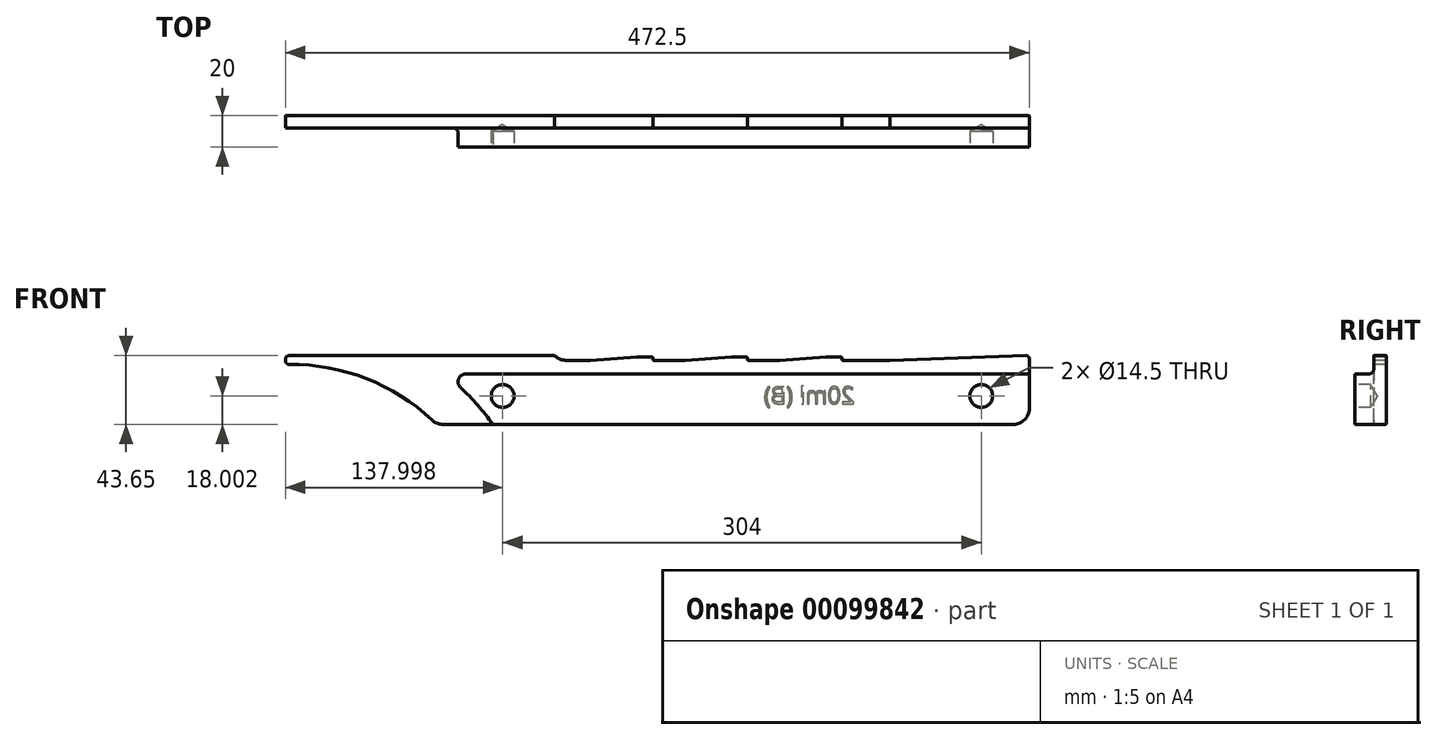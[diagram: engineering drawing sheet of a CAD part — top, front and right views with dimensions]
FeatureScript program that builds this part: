
annotation { "Feature Type Name" : "Feature", "Feature Type Description" : "" }
export const myFeature = defineFeature(function(context is Context, id is Id, definition is map)
    precondition{}
    {
        {
            var Q0;
            Q0=qCreatedBy(makeId("Front.planeOp"),FACE);
            var sketch = newSketch(context, id + "F0", { "sketchPlane" : qUnion([Q0])});
            skFitSpline(sketch, "E0", {"points": [v(183.92, 49.12) * mm, v(184, 49.11) * mm, v(184.18, 49.07) * mm, v(184.37, 48.88) * mm, v(184.42, 48.7) * mm, v(184.42, 48.62) * mm]});
            skLineSegment(sketch, "E1", {"start": v(184.42, 48.62) * mm, "end": v(184.42, 29.12) * mm});
            skLineSegment(sketch, "E2", {"start": v(184.42, 29.12) * mm, "end": v(161.17, 29.12) * mm});
            skLineSegment(sketch, "E3", {"start": v(161.17, 29.12) * mm, "end": v(161.17, 43.12) * mm});
            skLineSegment(sketch, "E4", {"start": v(161.17, 43.12) * mm, "end": v(146.67, 43.12) * mm});
            skLineSegment(sketch, "E5", {"start": v(146.67, 43.12) * mm, "end": v(146.67, 29.12) * mm});
            skLineSegment(sketch, "E6", {"start": v(146.67, 29.12) * mm, "end": v(129.51, 29.12) * mm});
            skFitSpline(sketch, "E7", {"points": [v(129.51, 29.12) * mm, v(128.82, 30.1) * mm, v(127.65, 32.27) * mm, v(126.67, 36.03) * mm, v(126.5, 40.27) * mm, v(127.13, 44.76) * mm, v(128.15, 47.72) * mm, v(128.8, 49.12) * mm]});
            skLineSegment(sketch, "E8", {"start": v(128.8, 49.12) * mm, "end": v(183.92, 49.12) * mm});
            skLineSegment(sketch, "E9", {"start": v(-288.08, -225.1) * mm, "end": v(-288.08, -225.75) * mm});
            skLineSegment(sketch, "E10", {"start": v(-287.58, -225.1) * mm, "end": v(-287.58, -225.75) * mm});
            skLineSegment(sketch, "E11", {"start": v(-285.58, -227.75) * mm, "end": v(-285.58, -228.25) * mm});
            skLineSegment(sketch, "E12", {"start": v(-285.58, -223.1) * mm, "end": v(-285.58, -222.6) * mm});
            skLineSegment(sketch, "E13", {"start": v(-284.08, -223.1) * mm, "end": v(-284.08, -222.6) * mm});
            skLineSegment(sketch, "E14", {"start": v(81.08, -203.54) * mm, "end": v(82.13, -203.33) * mm});
            skLineSegment(sketch, "E15", {"start": v(71.5, -203.54) * mm, "end": v(72.54, -203.33) * mm});
            skLineSegment(sketch, "E16", {"start": v(71.5, -195.67) * mm, "end": v(70.46, -195.88) * mm});
            skLineSegment(sketch, "E17", {"start": v(71.5, -204.6) * mm, "end": v(72.75, -204.39) * mm});
            skLineSegment(sketch, "E18", {"start": v(82.33, -204.39) * mm, "end": v(80.88, -204.6) * mm});
            skLineSegment(sketch, "E19", {"start": v(-285.58, -228.25) * mm, "end": v(-117.08, -228.25) * mm});
            skLineSegment(sketch, "E20", {"start": v(24.42, -194.81) * mm, "end": v(25.46, -194.6) * mm});
            skLineSegment(sketch, "E21", {"start": v(71.5, -194.6) * mm, "end": v(70.25, -194.81) * mm});
            skLineSegment(sketch, "E22", {"start": v(-285.58, -227.75) * mm, "end": v(-117.29, -227.75) * mm});
            skLineSegment(sketch, "E23", {"start": v(-64.42, -227.25) * mm, "end": v(-55.08, -227.25) * mm});
            skLineSegment(sketch, "E24", {"start": v(-4.42, -227.25) * mm, "end": v(4.92, -227.25) * mm});
            skLineSegment(sketch, "E25", {"start": v(55.58, -227.25) * mm, "end": v(64.92, -227.25) * mm});
            skLineSegment(sketch, "E26", {"start": v(-64.42, -226.75) * mm, "end": v(-54.58, -226.75) * mm});
            skLineSegment(sketch, "E27", {"start": v(-4.42, -226.75) * mm, "end": v(5.42, -226.75) * mm});
            skLineSegment(sketch, "E28", {"start": v(55.58, -226.75) * mm, "end": v(65.42, -226.75) * mm});
            skLineSegment(sketch, "E29", {"start": v(183.92, -226.25) * mm, "end": v(184.42, -226.25) * mm});
            skLineSegment(sketch, "E30", {"start": v(-55.08, -225.75) * mm, "end": v(-54.58, -225.75) * mm});
            skLineSegment(sketch, "E31", {"start": v(4.92, -225.75) * mm, "end": v(5.42, -225.75) * mm});
            skLineSegment(sketch, "E32", {"start": v(64.92, -225.75) * mm, "end": v(65.42, -225.75) * mm});
            skLineSegment(sketch, "E33", {"start": v(-287.58, -225.75) * mm, "end": v(-288.08, -225.75) * mm});
            skLineSegment(sketch, "E34", {"start": v(-109.94, -225.25) * mm, "end": v(-94.75, -225.25) * mm});
            skLineSegment(sketch, "E35", {"start": v(-54.08, -225.25) * mm, "end": v(-34.75, -225.25) * mm});
            skLineSegment(sketch, "E36", {"start": v(5.92, -225.25) * mm, "end": v(25.25, -225.25) * mm});
            skLineSegment(sketch, "E37", {"start": v(65.92, -225.25) * mm, "end": v(95.92, -225.25) * mm});
            skLineSegment(sketch, "E38", {"start": v(-287.58, -225.1) * mm, "end": v(-288.08, -225.1) * mm});
            skLineSegment(sketch, "E39", {"start": v(-109.94, -224.75) * mm, "end": v(-94.75, -224.75) * mm});
            skLineSegment(sketch, "E40", {"start": v(-54.08, -224.75) * mm, "end": v(-34.75, -224.75) * mm});
            skLineSegment(sketch, "E41", {"start": v(5.92, -224.75) * mm, "end": v(25.25, -224.75) * mm});
            skLineSegment(sketch, "E42", {"start": v(65.92, -224.75) * mm, "end": v(95.93, -224.75) * mm});
            skLineSegment(sketch, "E43", {"start": v(-284.08, -223.1) * mm, "end": v(-285.58, -223.1) * mm});
            skLineSegment(sketch, "E44", {"start": v(-284.08, -222.6) * mm, "end": v(-285.58, -222.6) * mm});
            skLineSegment(sketch, "E45", {"start": v(-94.75, -225.25) * mm, "end": v(-94.42, -225.26) * mm});
            skLineSegment(sketch, "E46", {"start": v(-34.75, -225.25) * mm, "end": v(-34.42, -225.26) * mm});
            skLineSegment(sketch, "E47", {"start": v(25.25, -225.25) * mm, "end": v(25.58, -225.26) * mm});
            skLineSegment(sketch, "E48", {"start": v(95.92, -225.25) * mm, "end": v(182.87, -228.2) * mm});
            skLineSegment(sketch, "E49", {"start": v(95.93, -224.75) * mm, "end": v(182.82, -227.7) * mm});
            skLineSegment(sketch, "E50", {"start": v(-94.42, -225.26) * mm, "end": v(-64.75, -227.24) * mm});
            skLineSegment(sketch, "E51", {"start": v(-94.38, -224.76) * mm, "end": v(-64.71, -226.74) * mm});
            skLineSegment(sketch, "E52", {"start": v(-34.42, -225.26) * mm, "end": v(-4.75, -227.24) * mm});
            skLineSegment(sketch, "E53", {"start": v(-34.38, -224.76) * mm, "end": v(-4.71, -226.74) * mm});
            skLineSegment(sketch, "E54", {"start": v(25.58, -225.26) * mm, "end": v(55.25, -227.24) * mm});
            skLineSegment(sketch, "E55", {"start": v(25.62, -224.76) * mm, "end": v(55.29, -226.74) * mm});
            skLineSegment(sketch, "E56", {"start": v(-194.7, -187.68) * mm, "end": v(-195.04, -187.32) * mm});
            skLineSegment(sketch, "E57", {"start": v(80.88, -204.6) * mm, "end": v(80.04, -204.6) * mm});
            skLineSegment(sketch, "E58", {"start": v(46.7, -204.6) * mm, "end": v(45.67, -204.6) * mm});
            skLineSegment(sketch, "E59", {"start": v(30.46, -204.6) * mm, "end": v(25.46, -204.6) * mm});
            skLineSegment(sketch, "E60", {"start": v(21.08, -204.6) * mm, "end": v(20.25, -204.6) * mm});
            skLineSegment(sketch, "E61", {"start": v(32.13, -204.6) * mm, "end": v(32.96, -204.6) * mm});
            skLineSegment(sketch, "E62", {"start": v(80.25, -203.54) * mm, "end": v(81.08, -203.54) * mm});
            skLineSegment(sketch, "E63", {"start": v(25.25, -203.33) * mm, "end": v(29.2, -203.33) * mm});
            skLineSegment(sketch, "E64", {"start": v(83.17, -202.26) * mm, "end": v(84.2, -202.26) * mm});
            skLineSegment(sketch, "E65", {"start": v(56.08, -201.41) * mm, "end": v(55.04, -201.41) * mm});
            skLineSegment(sketch, "E66", {"start": v(54, -201.41) * mm, "end": v(53.17, -201.41) * mm});
            skLineSegment(sketch, "E67", {"start": v(50.67, -201.41) * mm, "end": v(49.83, -201.41) * mm});
            skLineSegment(sketch, "E68", {"start": v(50.25, -200.56) * mm, "end": v(50.88, -200.56) * mm});
            skLineSegment(sketch, "E69", {"start": v(53.58, -200.56) * mm, "end": v(54, -200.56) * mm});
            skLineSegment(sketch, "E70", {"start": v(29.2, -200.35) * mm, "end": v(25.25, -200.35) * mm});
            skLineSegment(sketch, "E71", {"start": v(29.2, -199.07) * mm, "end": v(25.25, -199.07) * mm});
            skLineSegment(sketch, "E72", {"start": v(25.25, -195.88) * mm, "end": v(29.2, -195.88) * mm});
            skLineSegment(sketch, "E73", {"start": v(82.75, -195.67) * mm, "end": v(76.92, -195.67) * mm});
            skLineSegment(sketch, "E74", {"start": v(25.46, -194.6) * mm, "end": v(30.46, -194.6) * mm});
            skLineSegment(sketch, "E75", {"start": v(45.67, -194.6) * mm, "end": v(46.7, -194.6) * mm});
            skLineSegment(sketch, "E76", {"start": v(48.38, -194.6) * mm, "end": v(49.42, -194.6) * mm});
            skLineSegment(sketch, "E77", {"start": v(51.7, -194.6) * mm, "end": v(52.75, -194.6) * mm});
            skLineSegment(sketch, "E78", {"start": v(55.04, -194.6) * mm, "end": v(56.08, -194.6) * mm});
            skLineSegment(sketch, "E79", {"start": v(76.92, -194.6) * mm, "end": v(84.42, -194.6) * mm});
            skLineSegment(sketch, "E80", {"start": v(183.92, -194.6) * mm, "end": v(184.42, -194.6) * mm});
            skLineSegment(sketch, "E81", {"start": v(32.96, -193.33) * mm, "end": v(32.13, -193.33) * mm});
            skLineSegment(sketch, "E82", {"start": v(20.25, -193.33) * mm, "end": v(21.08, -193.33) * mm});
            skLineSegment(sketch, "E83", {"start": v(174.42, -185.1) * mm, "end": v(-188.19, -185.1) * mm});
            skLineSegment(sketch, "E84", {"start": v(174.42, -184.6) * mm, "end": v(-188.19, -184.6) * mm});
            skLineSegment(sketch, "E85", {"start": v(-117.18, -228) * mm, "end": v(-117.01, -228.18) * mm});
            skLineSegment(sketch, "E86", {"start": v(70.25, -204.39) * mm, "end": v(71.5, -204.6) * mm});
            skLineSegment(sketch, "E87", {"start": v(80.04, -204.6) * mm, "end": v(78.8, -204.39) * mm});
            skLineSegment(sketch, "E88", {"start": v(72.75, -194.81) * mm, "end": v(71.5, -194.6) * mm});
            skLineSegment(sketch, "E89", {"start": v(25.46, -204.6) * mm, "end": v(24.42, -204.39) * mm});
            skLineSegment(sketch, "E90", {"start": v(70.46, -203.33) * mm, "end": v(71.5, -203.54) * mm});
            skLineSegment(sketch, "E91", {"start": v(79.2, -203.33) * mm, "end": v(80.25, -203.54) * mm});
            skLineSegment(sketch, "E92", {"start": v(-188.19, -185.1) * mm, "end": v(-188.19, -184.6) * mm});
            skLineSegment(sketch, "E93", {"start": v(72.54, -195.88) * mm, "end": v(71.5, -195.67) * mm});
            skLineSegment(sketch, "E94", {"start": v(24.63, -203.11) * mm, "end": v(25.25, -203.33) * mm});
            skLineSegment(sketch, "E95", {"start": v(25.25, -199.07) * mm, "end": v(24.63, -198.86) * mm});
            skLineSegment(sketch, "E96", {"start": v(49.83, -201.41) * mm, "end": v(49.2, -201.2) * mm});
            skLineSegment(sketch, "E97", {"start": v(53.17, -201.41) * mm, "end": v(52.54, -201.2) * mm});
            skLineSegment(sketch, "E98", {"start": v(24, -199.7) * mm, "end": v(23.58, -199.5) * mm});
            skLineSegment(sketch, "E99", {"start": v(49.83, -200.35) * mm, "end": v(50.25, -200.56) * mm});
            skLineSegment(sketch, "E100", {"start": v(53.17, -200.35) * mm, "end": v(53.58, -200.56) * mm});
            skLineSegment(sketch, "E101", {"start": v(78.8, -204.39) * mm, "end": v(77.96, -203.96) * mm});
            skLineSegment(sketch, "E102", {"start": v(24.42, -204.39) * mm, "end": v(23.58, -203.75) * mm});
            skLineSegment(sketch, "E103", {"start": v(-109.94, -224.75) * mm, "end": v(-109.94, -225.25) * mm});
            skLineSegment(sketch, "E104", {"start": v(69.2, -203.75) * mm, "end": v(70.25, -204.39) * mm});
            skLineSegment(sketch, "E105", {"start": v(73.8, -195.45) * mm, "end": v(72.75, -194.81) * mm});
            skLineSegment(sketch, "E106", {"start": v(69.83, -202.9) * mm, "end": v(70.46, -203.33) * mm});
            skLineSegment(sketch, "E107", {"start": v(78.58, -202.9) * mm, "end": v(79.2, -203.33) * mm});
            skLineSegment(sketch, "E108", {"start": v(-94.75, -224.75) * mm, "end": v(-94.75, -225.25) * mm});
            skLineSegment(sketch, "E109", {"start": v(-94.38, -224.76) * mm, "end": v(-94.42, -225.26) * mm});
            skLineSegment(sketch, "E110", {"start": v(73.17, -196.3) * mm, "end": v(72.54, -195.88) * mm});
            skLineSegment(sketch, "E111", {"start": v(24.2, -202.69) * mm, "end": v(24.63, -203.11) * mm});
            skLineSegment(sketch, "E112", {"start": v(24.63, -198.86) * mm, "end": v(24.2, -198.43) * mm});
            skLineSegment(sketch, "E113", {"start": v(-64.42, -226.75) * mm, "end": v(-64.42, -227.25) * mm});
            skLineSegment(sketch, "E114", {"start": v(-55.08, -227.25) * mm, "end": v(-55.08, -225.75) * mm});
            skLineSegment(sketch, "E115", {"start": v(-54.58, -226.75) * mm, "end": v(-54.58, -225.75) * mm});
            skLineSegment(sketch, "E116", {"start": v(-54.08, -224.75) * mm, "end": v(-54.08, -225.25) * mm});
            skLineSegment(sketch, "E117", {"start": v(-64.71, -226.74) * mm, "end": v(-64.75, -227.24) * mm});
            skLineSegment(sketch, "E118", {"start": v(49.2, -201.2) * mm, "end": v(48.8, -200.77) * mm});
            skLineSegment(sketch, "E119", {"start": v(49.63, -200.13) * mm, "end": v(49.83, -200.35) * mm});
            skLineSegment(sketch, "E120", {"start": v(52.54, -201.2) * mm, "end": v(51.92, -200.56) * mm});
            skLineSegment(sketch, "E121", {"start": v(52.96, -200.13) * mm, "end": v(53.17, -200.35) * mm});
            skLineSegment(sketch, "E122", {"start": v(68.58, -203.11) * mm, "end": v(69.2, -203.75) * mm});
            skLineSegment(sketch, "E123", {"start": v(77.96, -203.96) * mm, "end": v(77.13, -203.11) * mm});
            skLineSegment(sketch, "E124", {"start": v(74.42, -196.1) * mm, "end": v(73.8, -195.45) * mm});
            skLineSegment(sketch, "E125", {"start": v(23.58, -203.75) * mm, "end": v(22.96, -202.9) * mm});
            skLineSegment(sketch, "E126", {"start": v(23.58, -199.5) * mm, "end": v(22.96, -198.64) * mm});
            skLineSegment(sketch, "E127", {"start": v(-34.75, -224.75) * mm, "end": v(-34.75, -225.25) * mm});
            skLineSegment(sketch, "E128", {"start": v(-34.38, -224.76) * mm, "end": v(-34.42, -225.26) * mm});
            skLineSegment(sketch, "E129", {"start": v(-117.08, -228.25) * mm, "end": v(-117.01, -228.18) * mm});
            skLineSegment(sketch, "E130", {"start": v(69, -201.62) * mm, "end": v(69.83, -202.9) * mm});
            skLineSegment(sketch, "E131", {"start": v(74, -197.58) * mm, "end": v(73.17, -196.3) * mm});
            skLineSegment(sketch, "E132", {"start": v(78.17, -202.26) * mm, "end": v(78.58, -202.9) * mm});
            skLineSegment(sketch, "E133", {"start": v(49.42, -199.7) * mm, "end": v(49.63, -200.13) * mm});
            skLineSegment(sketch, "E134", {"start": v(52.75, -199.7) * mm, "end": v(52.96, -200.13) * mm});
            skLineSegment(sketch, "E135", {"start": v(20.25, -204.6) * mm, "end": v(19.83, -203.54) * mm});
            skLineSegment(sketch, "E136", {"start": v(20.67, -203.54) * mm, "end": v(21.08, -204.6) * mm});
            skLineSegment(sketch, "E137", {"start": v(32.13, -193.33) * mm, "end": v(32.54, -194.39) * mm});
            skLineSegment(sketch, "E138", {"start": v(33.38, -194.39) * mm, "end": v(32.96, -193.33) * mm});
            skLineSegment(sketch, "E139", {"start": v(22.96, -202.9) * mm, "end": v(22.75, -202.26) * mm});
            skLineSegment(sketch, "E140", {"start": v(24, -202.05) * mm, "end": v(24.2, -202.69) * mm});
            skLineSegment(sketch, "E141", {"start": v(22.96, -198.64) * mm, "end": v(22.75, -198) * mm});
            skLineSegment(sketch, "E142", {"start": v(24.2, -198.43) * mm, "end": v(24, -197.8) * mm});
            skLineSegment(sketch, "E143", {"start": v(19.42, -201.62) * mm, "end": v(19.2, -199.7) * mm});
            skLineSegment(sketch, "E144", {"start": v(20.04, -199.7) * mm, "end": v(20.25, -201.62) * mm});
            skLineSegment(sketch, "E145", {"start": v(-4.42, -226.75) * mm, "end": v(-4.42, -227.25) * mm});
            skLineSegment(sketch, "E146", {"start": v(4.92, -227.25) * mm, "end": v(4.92, -225.75) * mm});
            skLineSegment(sketch, "E147", {"start": v(5.42, -226.75) * mm, "end": v(5.42, -225.75) * mm});
            skLineSegment(sketch, "E148", {"start": v(5.92, -224.75) * mm, "end": v(5.92, -225.25) * mm});
            skLineSegment(sketch, "E149", {"start": v(-4.71, -226.74) * mm, "end": v(-4.75, -227.24) * mm});
            skLineSegment(sketch, "E150", {"start": v(68.17, -202.26) * mm, "end": v(68.58, -203.11) * mm});
            skLineSegment(sketch, "E151", {"start": v(74.83, -196.94) * mm, "end": v(74.42, -196.1) * mm});
            skLineSegment(sketch, "E152", {"start": v(48.8, -200.77) * mm, "end": v(48.38, -199.7) * mm});
            skLineSegment(sketch, "E153", {"start": v(19.83, -203.54) * mm, "end": v(19.42, -201.62) * mm});
            skLineSegment(sketch, "E154", {"start": v(20.25, -201.62) * mm, "end": v(20.67, -203.54) * mm});
            skLineSegment(sketch, "E155", {"start": v(32.54, -194.39) * mm, "end": v(32.96, -196.3) * mm});
            skLineSegment(sketch, "E156", {"start": v(33.8, -196.3) * mm, "end": v(33.38, -194.39) * mm});
            skLineSegment(sketch, "E157", {"start": v(32.96, -196.3) * mm, "end": v(33.17, -198.22) * mm});
            skLineSegment(sketch, "E158", {"start": v(34, -198.22) * mm, "end": v(33.8, -196.3) * mm});
            skLineSegment(sketch, "E159", {"start": v(19.2, -199.7) * mm, "end": v(19.2, -198.22) * mm});
            skLineSegment(sketch, "E160", {"start": v(20.04, -198.22) * mm, "end": v(20.04, -199.7) * mm});
            skLineSegment(sketch, "E161", {"start": v(22.75, -202.26) * mm, "end": v(22.75, -201.41) * mm});
            skLineSegment(sketch, "E162", {"start": v(22.75, -198) * mm, "end": v(22.75, -196.94) * mm});
            skLineSegment(sketch, "E163", {"start": v(24, -201.62) * mm, "end": v(24, -202.05) * mm});
            skLineSegment(sketch, "E164", {"start": v(24, -197.8) * mm, "end": v(24, -197.16) * mm});
            skLineSegment(sketch, "E165", {"start": v(25.25, -224.75) * mm, "end": v(25.25, -225.25) * mm});
            skLineSegment(sketch, "E166", {"start": v(29.2, -195.88) * mm, "end": v(29.2, -199.07) * mm});
            skLineSegment(sketch, "E167", {"start": v(29.2, -203.33) * mm, "end": v(29.2, -200.35) * mm});
            skLineSegment(sketch, "E168", {"start": v(30.46, -194.6) * mm, "end": v(30.46, -204.6) * mm});
            skLineSegment(sketch, "E169", {"start": v(33.17, -198.22) * mm, "end": v(33.17, -199.7) * mm});
            skLineSegment(sketch, "E170", {"start": v(34, -199.7) * mm, "end": v(34, -198.22) * mm});
            skLineSegment(sketch, "E171", {"start": v(25.62, -224.76) * mm, "end": v(25.58, -225.26) * mm});
            skLineSegment(sketch, "E172", {"start": v(19.2, -198.22) * mm, "end": v(19.42, -196.3) * mm});
            skLineSegment(sketch, "E173", {"start": v(20.25, -196.3) * mm, "end": v(20.04, -198.22) * mm});
            skLineSegment(sketch, "E174", {"start": v(19.42, -196.3) * mm, "end": v(19.83, -194.39) * mm});
            skLineSegment(sketch, "E175", {"start": v(23.58, -199.92) * mm, "end": v(24, -199.7) * mm});
            skLineSegment(sketch, "E176", {"start": v(24.63, -196.1) * mm, "end": v(25.25, -195.88) * mm});
            skLineSegment(sketch, "E177", {"start": v(25.25, -200.35) * mm, "end": v(24.63, -200.56) * mm});
            skLineSegment(sketch, "E178", {"start": v(51.3, -201.2) * mm, "end": v(50.67, -201.41) * mm});
            skLineSegment(sketch, "E179", {"start": v(54, -200.56) * mm, "end": v(54.63, -200.35) * mm});
            skLineSegment(sketch, "E180", {"start": v(54.63, -201.2) * mm, "end": v(54, -201.41) * mm});
            skLineSegment(sketch, "E181", {"start": v(67.96, -201.62) * mm, "end": v(68.17, -202.26) * mm});
            skLineSegment(sketch, "E182", {"start": v(75.04, -197.58) * mm, "end": v(74.83, -196.94) * mm});
            skLineSegment(sketch, "E183", {"start": v(45.67, -204.6) * mm, "end": v(45.67, -194.6) * mm});
            skLineSegment(sketch, "E184", {"start": v(46.7, -194.6) * mm, "end": v(46.7, -204.6) * mm});
            skLineSegment(sketch, "E185", {"start": v(48.38, -199.7) * mm, "end": v(48.38, -194.6) * mm});
            skLineSegment(sketch, "E186", {"start": v(49.42, -194.6) * mm, "end": v(49.42, -199.7) * mm});
            skLineSegment(sketch, "E187", {"start": v(51.7, -199.7) * mm, "end": v(51.7, -194.6) * mm});
            skLineSegment(sketch, "E188", {"start": v(52.75, -194.6) * mm, "end": v(52.75, -199.7) * mm});
            skLineSegment(sketch, "E189", {"start": v(55.04, -201.41) * mm, "end": v(55.04, -200.77) * mm});
            skLineSegment(sketch, "E190", {"start": v(55.04, -199.92) * mm, "end": v(55.04, -194.6) * mm});
            skLineSegment(sketch, "E191", {"start": v(55.58, -226.75) * mm, "end": v(55.58, -227.25) * mm});
            skLineSegment(sketch, "E192", {"start": v(56.08, -194.6) * mm, "end": v(56.08, -201.41) * mm});
            skLineSegment(sketch, "E193", {"start": v(33.17, -199.7) * mm, "end": v(32.96, -201.62) * mm});
            skLineSegment(sketch, "E194", {"start": v(33.8, -201.62) * mm, "end": v(34, -199.7) * mm});
            skLineSegment(sketch, "E195", {"start": v(20.67, -194.39) * mm, "end": v(20.25, -196.3) * mm});
            skLineSegment(sketch, "E196", {"start": v(32.96, -201.62) * mm, "end": v(32.54, -203.54) * mm});
            skLineSegment(sketch, "E197", {"start": v(33.38, -203.54) * mm, "end": v(33.8, -201.62) * mm});
            skLineSegment(sketch, "E198", {"start": v(22.75, -196.94) * mm, "end": v(22.96, -196.3) * mm});
            skLineSegment(sketch, "E199", {"start": v(24, -197.16) * mm, "end": v(24.2, -196.52) * mm});
            skLineSegment(sketch, "E200", {"start": v(22.75, -201.41) * mm, "end": v(22.96, -200.77) * mm});
            skLineSegment(sketch, "E201", {"start": v(24.2, -200.98) * mm, "end": v(24, -201.62) * mm});
            skLineSegment(sketch, "E202", {"start": v(19.83, -194.39) * mm, "end": v(20.25, -193.33) * mm});
            skLineSegment(sketch, "E203", {"start": v(21.08, -193.33) * mm, "end": v(20.67, -194.39) * mm});
            skLineSegment(sketch, "E204", {"start": v(22.96, -196.3) * mm, "end": v(23.58, -195.45) * mm});
            skLineSegment(sketch, "E205", {"start": v(22.96, -200.77) * mm, "end": v(23.58, -199.92) * mm});
            skLineSegment(sketch, "E206", {"start": v(24.2, -196.52) * mm, "end": v(24.63, -196.1) * mm});
            skLineSegment(sketch, "E207", {"start": v(24.63, -200.56) * mm, "end": v(24.2, -200.98) * mm});
            skLineSegment(sketch, "E208", {"start": v(23.58, -195.45) * mm, "end": v(24.42, -194.81) * mm});
            skLineSegment(sketch, "E209", {"start": v(50.88, -200.56) * mm, "end": v(51.3, -200.35) * mm});
            skLineSegment(sketch, "E210", {"start": v(77.13, -203.11) * mm, "end": v(76.92, -202.26) * mm});
            skLineSegment(sketch, "E211", {"start": v(67.75, -200.56) * mm, "end": v(67.96, -201.62) * mm});
            skLineSegment(sketch, "E212", {"start": v(75.25, -198.64) * mm, "end": v(75.04, -197.58) * mm});
            skLineSegment(sketch, "E213", {"start": v(68.8, -200.35) * mm, "end": v(69, -201.62) * mm});
            skLineSegment(sketch, "E214", {"start": v(74.2, -198.86) * mm, "end": v(74, -197.58) * mm});
            skLineSegment(sketch, "E215", {"start": v(64.92, -227.25) * mm, "end": v(64.92, -225.75) * mm});
            skLineSegment(sketch, "E216", {"start": v(65.42, -226.75) * mm, "end": v(65.42, -225.75) * mm});
            skLineSegment(sketch, "E217", {"start": v(65.92, -224.75) * mm, "end": v(65.92, -225.25) * mm});
            skLineSegment(sketch, "E218", {"start": v(67.75, -198.64) * mm, "end": v(67.75, -200.56) * mm});
            skLineSegment(sketch, "E219", {"start": v(68.8, -198.86) * mm, "end": v(68.8, -200.35) * mm});
            skLineSegment(sketch, "E220", {"start": v(74.2, -200.35) * mm, "end": v(74.2, -198.86) * mm});
            skLineSegment(sketch, "E221", {"start": v(75.25, -200.56) * mm, "end": v(75.25, -198.64) * mm});
            skLineSegment(sketch, "E222", {"start": v(76.92, -202.26) * mm, "end": v(76.92, -201.84) * mm});
            skLineSegment(sketch, "E223", {"start": v(76.92, -195.67) * mm, "end": v(76.92, -194.6) * mm});
            skLineSegment(sketch, "E224", {"start": v(78.17, -201.84) * mm, "end": v(78.17, -202.26) * mm});
            skLineSegment(sketch, "E225", {"start": v(84.42, -194.6) * mm, "end": v(84.42, -195.67) * mm});
            skLineSegment(sketch, "E226", {"start": v(55.29, -226.74) * mm, "end": v(55.25, -227.24) * mm});
            skLineSegment(sketch, "E227", {"start": v(69, -197.58) * mm, "end": v(68.8, -198.86) * mm});
            skLineSegment(sketch, "E228", {"start": v(67.96, -197.58) * mm, "end": v(67.75, -198.64) * mm});
            skLineSegment(sketch, "E229", {"start": v(32.54, -203.54) * mm, "end": v(32.13, -204.6) * mm});
            skLineSegment(sketch, "E230", {"start": v(32.96, -204.6) * mm, "end": v(33.38, -203.54) * mm});
            skLineSegment(sketch, "E231", {"start": v(51.5, -200.13) * mm, "end": v(51.7, -199.7) * mm});
            skLineSegment(sketch, "E232", {"start": v(51.3, -200.35) * mm, "end": v(51.5, -200.13) * mm});
            skLineSegment(sketch, "E233", {"start": v(51.92, -200.56) * mm, "end": v(51.3, -201.2) * mm});
            skLineSegment(sketch, "E234", {"start": v(54.63, -200.35) * mm, "end": v(55.04, -199.92) * mm});
            skLineSegment(sketch, "E235", {"start": v(55.04, -200.77) * mm, "end": v(54.63, -201.2) * mm});
            skLineSegment(sketch, "E236", {"start": v(70.46, -195.88) * mm, "end": v(69.83, -196.3) * mm});
            skLineSegment(sketch, "E237", {"start": v(72.54, -203.33) * mm, "end": v(73.17, -202.9) * mm});
            skLineSegment(sketch, "E238", {"start": v(82.13, -203.33) * mm, "end": v(82.75, -202.9) * mm});
            skLineSegment(sketch, "E239", {"start": v(70.25, -194.81) * mm, "end": v(69.2, -195.45) * mm});
            skLineSegment(sketch, "E240", {"start": v(72.75, -204.39) * mm, "end": v(73.8, -203.75) * mm});
            skLineSegment(sketch, "E241", {"start": v(83.17, -203.96) * mm, "end": v(82.33, -204.39) * mm});
            skLineSegment(sketch, "E242", {"start": v(74, -201.62) * mm, "end": v(74.2, -200.35) * mm});
            skLineSegment(sketch, "E243", {"start": v(75.04, -201.62) * mm, "end": v(75.25, -200.56) * mm});
            skLineSegment(sketch, "E244", {"start": v(76.92, -201.84) * mm, "end": v(77.13, -200.98) * mm});
            skLineSegment(sketch, "E245", {"start": v(84.2, -202.26) * mm, "end": v(84, -203.11) * mm});
            skLineSegment(sketch, "E246", {"start": v(68.17, -196.94) * mm, "end": v(67.96, -197.58) * mm});
            skLineSegment(sketch, "E247", {"start": v(74.83, -202.26) * mm, "end": v(75.04, -201.62) * mm});
            skLineSegment(sketch, "E248", {"start": v(68.58, -196.1) * mm, "end": v(68.17, -196.94) * mm});
            skLineSegment(sketch, "E249", {"start": v(74.42, -203.11) * mm, "end": v(74.83, -202.26) * mm});
            skLineSegment(sketch, "E250", {"start": v(78.58, -200.98) * mm, "end": v(78.17, -201.84) * mm});
            skLineSegment(sketch, "E251", {"start": v(69.83, -196.3) * mm, "end": v(69, -197.58) * mm});
            skLineSegment(sketch, "E252", {"start": v(73.17, -202.9) * mm, "end": v(74, -201.62) * mm});
            skLineSegment(sketch, "E253", {"start": v(77.13, -200.98) * mm, "end": v(77.54, -200.35) * mm});
            skLineSegment(sketch, "E254", {"start": v(69.2, -195.45) * mm, "end": v(68.58, -196.1) * mm});
            skLineSegment(sketch, "E255", {"start": v(73.8, -203.75) * mm, "end": v(74.42, -203.11) * mm});
            skLineSegment(sketch, "E256", {"start": v(84, -203.11) * mm, "end": v(83.17, -203.96) * mm});
            skLineSegment(sketch, "E257", {"start": v(84.42, -195.67) * mm, "end": v(78.58, -200.98) * mm});
            skLineSegment(sketch, "E258", {"start": v(77.54, -200.35) * mm, "end": v(82.75, -195.67) * mm});
            skLineSegment(sketch, "E259", {"start": v(82.75, -202.9) * mm, "end": v(83.17, -202.26) * mm});
            skLineSegment(sketch, "E260", {"start": v(174.42, -185.1) * mm, "end": v(174.42, -184.6) * mm});
            skLineSegment(sketch, "E261", {"start": v(183.92, -226.25) * mm, "end": v(183.92, -194.6) * mm});
            skLineSegment(sketch, "E262", {"start": v(184.42, -226.25) * mm, "end": v(184.42, -194.6) * mm});
            skLineSegment(sketch, "E263", {"start": v(-288.08, 48.62) * mm, "end": v(-288.08, 41.12) * mm});
            skLineSegment(sketch, "E264", {"start": v(-285.58, 49.12) * mm, "end": v(-285.58, 41.12) * mm});
            skLineSegment(sketch, "E265", {"start": v(-178.42, 29.12) * mm, "end": v(-178.42, 38.12) * mm});
            skLineSegment(sketch, "E266", {"start": v(-173.42, 29.12) * mm, "end": v(-173.42, 41.12) * mm});
            skLineSegment(sketch, "E267", {"start": v(-178.42, 29.12) * mm, "end": v(184.42, 29.12) * mm});
            skLineSegment(sketch, "E268", {"start": v(126.84, 38.12) * mm, "end": v(-178.42, 38.12) * mm});
            skLineSegment(sketch, "E269", {"start": v(145.92, 39.12) * mm, "end": v(161.92, 39.12) * mm});
            skLineSegment(sketch, "E270", {"start": v(-288.08, 41.12) * mm, "end": v(126.8, 41.12) * mm});
            skLineSegment(sketch, "E271", {"start": v(-117.08, 48.62) * mm, "end": v(-117.1, 48.78) * mm});
            skLineSegment(sketch, "E272", {"start": v(-117.1, 48.78) * mm, "end": v(-117.13, 48.93) * mm});
            skLineSegment(sketch, "E273", {"start": v(-117.13, 48.93) * mm, "end": v(-117.18, 49.04) * mm});
            skLineSegment(sketch, "E274", {"start": v(-117.08, 41.12) * mm, "end": v(-117.08, 48.62) * mm});
            skLineSegment(sketch, "E275", {"start": v(-117.01, 48.62) * mm, "end": v(-117.01, 41.12) * mm});
            skLineSegment(sketch, "E276", {"start": v(-109.94, 49.12) * mm, "end": v(-109.94, 41.12) * mm});
            skLineSegment(sketch, "E277", {"start": v(146.67, 43.12) * mm, "end": v(161.17, 43.12) * mm});
            skLineSegment(sketch, "E278", {"start": v(-288.08, 48.62) * mm, "end": v(-54.58, 48.62) * mm});
            skLineSegment(sketch, "E279", {"start": v(-54.52, 48.62) * mm, "end": v(5.42, 48.62) * mm});
            skLineSegment(sketch, "E280", {"start": v(5.48, 48.62) * mm, "end": v(65.42, 48.62) * mm});
            skLineSegment(sketch, "E281", {"start": v(65.48, 48.62) * mm, "end": v(128.81, 48.62) * mm});
            skLineSegment(sketch, "E282", {"start": v(-287.58, 49.12) * mm, "end": v(183.92, 49.12) * mm});
            skLineSegment(sketch, "E283", {"start": v(-117.18, 49.04) * mm, "end": v(-117.22, 49.08) * mm});
            skLineSegment(sketch, "E284", {"start": v(-117.22, 49.08) * mm, "end": v(-117.25, 49.1) * mm});
            skLineSegment(sketch, "E285", {"start": v(-117.25, 49.1) * mm, "end": v(-117.29, 49.12) * mm});
            skLineSegment(sketch, "E286", {"start": v(-117.18, 49.04) * mm, "end": v(-117.1, 48.93) * mm});
            skLineSegment(sketch, "E287", {"start": v(-117.1, 48.93) * mm, "end": v(-117.03, 48.78) * mm});
            skLineSegment(sketch, "E288", {"start": v(-117.03, 48.78) * mm, "end": v(-117.01, 48.62) * mm});
            skLineSegment(sketch, "E289", {"start": v(-94.75, 49.12) * mm, "end": v(-94.75, 41.12) * mm});
            skLineSegment(sketch, "E290", {"start": v(-94.42, 48.62) * mm, "end": v(-94.42, 41.12) * mm});
            skLineSegment(sketch, "E291", {"start": v(-94.41, 48.87) * mm, "end": v(-94.42, 48.62) * mm});
            skLineSegment(sketch, "E292", {"start": v(-94.38, 49.12) * mm, "end": v(-94.4, 49.05) * mm});
            skLineSegment(sketch, "E293", {"start": v(-94.4, 49.05) * mm, "end": v(-94.41, 48.87) * mm});
            skLineSegment(sketch, "E294", {"start": v(-64.75, 48.62) * mm, "end": v(-64.75, 41.12) * mm});
            skLineSegment(sketch, "E295", {"start": v(-64.42, 49.12) * mm, "end": v(-64.42, 41.12) * mm});
            skLineSegment(sketch, "E296", {"start": v(-64.74, 48.87) * mm, "end": v(-64.75, 48.62) * mm});
            skLineSegment(sketch, "E297", {"start": v(-64.71, 49.12) * mm, "end": v(-64.73, 49.05) * mm});
            skLineSegment(sketch, "E298", {"start": v(-64.73, 49.05) * mm, "end": v(-64.74, 48.87) * mm});
            skLineSegment(sketch, "E299", {"start": v(-55.08, 49.12) * mm, "end": v(-55.08, 41.12) * mm});
            skLineSegment(sketch, "E300", {"start": v(-54.58, 48.62) * mm, "end": v(-54.58, 41.12) * mm});
            skLineSegment(sketch, "E301", {"start": v(-54.08, 41.12) * mm, "end": v(-54.08, 49.12) * mm});
            skLineSegment(sketch, "E302", {"start": v(-34.75, 49.12) * mm, "end": v(-34.75, 41.12) * mm});
            skLineSegment(sketch, "E303", {"start": v(-34.42, 48.62) * mm, "end": v(-34.42, 41.12) * mm});
            skLineSegment(sketch, "E304", {"start": v(-34.41, 48.87) * mm, "end": v(-34.42, 48.62) * mm});
            skLineSegment(sketch, "E305", {"start": v(-34.38, 49.12) * mm, "end": v(-34.4, 49.05) * mm});
            skLineSegment(sketch, "E306", {"start": v(-34.4, 49.05) * mm, "end": v(-34.41, 48.87) * mm});
            skLineSegment(sketch, "E307", {"start": v(-4.75, 48.62) * mm, "end": v(-4.75, 41.12) * mm});
            skLineSegment(sketch, "E308", {"start": v(-4.42, 49.12) * mm, "end": v(-4.42, 41.12) * mm});
            skLineSegment(sketch, "E309", {"start": v(-4.74, 48.87) * mm, "end": v(-4.75, 48.62) * mm});
            skLineSegment(sketch, "E310", {"start": v(-4.71, 49.12) * mm, "end": v(-4.73, 49.05) * mm});
            skLineSegment(sketch, "E311", {"start": v(-4.73, 49.05) * mm, "end": v(-4.74, 48.87) * mm});
            skLineSegment(sketch, "E312", {"start": v(4.92, 49.12) * mm, "end": v(4.92, 41.12) * mm});
            skLineSegment(sketch, "E313", {"start": v(5.42, 48.62) * mm, "end": v(5.42, 41.12) * mm});
            skLineSegment(sketch, "E314", {"start": v(5.92, 41.12) * mm, "end": v(5.92, 49.12) * mm});
            skLineSegment(sketch, "E315", {"start": v(25.62, 49.12) * mm, "end": v(25.6, 49.05) * mm});
            skLineSegment(sketch, "E316", {"start": v(25.6, 49.05) * mm, "end": v(25.59, 48.87) * mm});
            skLineSegment(sketch, "E317", {"start": v(25.25, 49.12) * mm, "end": v(25.25, 41.12) * mm});
            skLineSegment(sketch, "E318", {"start": v(25.58, 48.62) * mm, "end": v(25.58, 41.12) * mm});
            skLineSegment(sketch, "E319", {"start": v(25.59, 48.87) * mm, "end": v(25.58, 48.62) * mm});
            skLineSegment(sketch, "E320", {"start": v(55.25, 48.62) * mm, "end": v(55.25, 41.12) * mm});
            skLineSegment(sketch, "E321", {"start": v(55.58, 49.12) * mm, "end": v(55.58, 41.12) * mm});
            skLineSegment(sketch, "E322", {"start": v(55.26, 48.87) * mm, "end": v(55.25, 48.62) * mm});
            skLineSegment(sketch, "E323", {"start": v(55.29, 49.12) * mm, "end": v(55.27, 49.05) * mm});
            skLineSegment(sketch, "E324", {"start": v(55.27, 49.05) * mm, "end": v(55.26, 48.87) * mm});
            skLineSegment(sketch, "E325", {"start": v(64.92, 49.12) * mm, "end": v(64.92, 41.12) * mm});
            skLineSegment(sketch, "E326", {"start": v(65.42, 48.62) * mm, "end": v(65.42, 41.12) * mm});
            skLineSegment(sketch, "E327", {"start": v(65.92, 41.12) * mm, "end": v(65.92, 49.12) * mm});
            skLineSegment(sketch, "E328", {"start": v(95.92, 48.62) * mm, "end": v(95.92, 48.87) * mm});
            skLineSegment(sketch, "E329", {"start": v(95.92, 48.87) * mm, "end": v(95.92, 49.05) * mm});
            skLineSegment(sketch, "E330", {"start": v(95.92, 49.05) * mm, "end": v(95.93, 49.12) * mm});
            skLineSegment(sketch, "E331", {"start": v(95.92, 48.62) * mm, "end": v(95.92, 41.12) * mm});
            skLineSegment(sketch, "E332", {"start": v(129.07, 49.12) * mm, "end": v(127.88, 46.8) * mm});
            skLineSegment(sketch, "E333", {"start": v(127.34, 33.64) * mm, "end": v(130.16, 29.12) * mm});
            skLineSegment(sketch, "E334", {"start": v(127.88, 46.8) * mm, "end": v(126.62, 40.11) * mm});
            skLineSegment(sketch, "E335", {"start": v(126.62, 40.11) * mm, "end": v(127.34, 33.64) * mm});
            skLineSegment(sketch, "E336", {"start": v(145.92, 39.12) * mm, "end": v(145.92, 29.12) * mm});
            skLineSegment(sketch, "E337", {"start": v(161.17, 43.12) * mm, "end": v(161.17, 29.12) * mm});
            skLineSegment(sketch, "E338", {"start": v(161.92, 39.12) * mm, "end": v(161.92, 29.12) * mm});
            skLineSegment(sketch, "E339", {"start": v(184.42, 29.12) * mm, "end": v(184.42, 48.62) * mm});
            skLineSegment(sketch, "E340", {"start": v(276.43, 29.12) * mm, "end": v(244.43, 29.12) * mm});
            skLineSegment(sketch, "E341", {"start": v(276.43, 38.12) * mm, "end": v(244.43, 38.12) * mm});
            skLineSegment(sketch, "E342", {"start": v(244.43, 41.12) * mm, "end": v(288.08, 41.12) * mm});
            skLineSegment(sketch, "E343", {"start": v(244.43, 48.62) * mm, "end": v(288.08, 48.62) * mm});
            skLineSegment(sketch, "E344", {"start": v(244.93, 49.12) * mm, "end": v(287.58, 49.12) * mm});
            skLineSegment(sketch, "E345", {"start": v(244.43, 29.12) * mm, "end": v(244.43, 48.62) * mm});
            skLineSegment(sketch, "E346", {"start": v(247.15, 41.12) * mm, "end": v(247.15, 48.62) * mm});
            skLineSegment(sketch, "E347", {"start": v(267.77, 29.12) * mm, "end": v(267.77, 38.12) * mm});
            skLineSegment(sketch, "E348", {"start": v(276.43, 29.12) * mm, "end": v(276.43, 38.12) * mm});
            skLineSegment(sketch, "E349", {"start": v(282.43, 48.62) * mm, "end": v(282.43, 41.12) * mm});
            skLineSegment(sketch, "E350", {"start": v(284.93, 49.12) * mm, "end": v(284.93, 41.12) * mm});
            skLineSegment(sketch, "E351", {"start": v(285.58, 49.12) * mm, "end": v(285.58, 41.12) * mm});
            skLineSegment(sketch, "E352", {"start": v(288.08, 48.62) * mm, "end": v(288.08, 41.12) * mm});
            skLineSegment(sketch, "E353", {"start": v(-288.08, 225.1) * mm, "end": v(-288.08, 225.75) * mm});
            skLineSegment(sketch, "E354", {"start": v(-178.87, 205.74) * mm, "end": v(-176.83, 207.94) * mm});
            skLineSegment(sketch, "E355", {"start": v(-173.42, 219.6) * mm, "end": v(-173.42, 216.6) * mm});
            skLineSegment(sketch, "E356", {"start": v(-150.08, 215.85) * mm, "end": v(-150.08, 218.6) * mm});
            skLineSegment(sketch, "E357", {"start": v(-54.58, 226.75) * mm, "end": v(-54.58, 225.75) * mm});
            skLineSegment(sketch, "E358", {"start": v(-188.19, 184.6) * mm, "end": v(174.42, 184.6) * mm});
            skLineSegment(sketch, "E359", {"start": v(-117.08, 228.25) * mm, "end": v(-117.01, 228.18) * mm});
            skLineSegment(sketch, "E360", {"start": v(5.42, 226.75) * mm, "end": v(5.42, 225.75) * mm});
            skLineSegment(sketch, "E361", {"start": v(25.58, 225.26) * mm, "end": v(55.25, 227.24) * mm});
            skLineSegment(sketch, "E362", {"start": v(-34.42, 225.26) * mm, "end": v(-4.75, 227.24) * mm});
            skLineSegment(sketch, "E363", {"start": v(-94.42, 225.26) * mm, "end": v(-64.75, 227.24) * mm});
            skLineSegment(sketch, "E364", {"start": v(182.87, 228.2) * mm, "end": v(95.92, 225.25) * mm});
            skLineSegment(sketch, "E365", {"start": v(184.42, 216.6) * mm, "end": v(-173.42, 216.6) * mm});
            skLineSegment(sketch, "E366", {"start": v(184.42, 219.6) * mm, "end": v(-173.42, 219.6) * mm});
            skLineSegment(sketch, "E367", {"start": v(-285.58, 222.6) * mm, "end": v(-284.08, 222.6) * mm});
            skLineSegment(sketch, "E368", {"start": v(95.92, 225.25) * mm, "end": v(65.92, 225.25) * mm});
            skLineSegment(sketch, "E369", {"start": v(25.25, 225.25) * mm, "end": v(5.92, 225.25) * mm});
            skLineSegment(sketch, "E370", {"start": v(-34.75, 225.25) * mm, "end": v(-54.08, 225.25) * mm});
            skLineSegment(sketch, "E371", {"start": v(-94.75, 225.25) * mm, "end": v(-109.94, 225.25) * mm});
            skLineSegment(sketch, "E372", {"start": v(-64.42, 227.25) * mm, "end": v(-55.08, 227.25) * mm});
            skLineSegment(sketch, "E373", {"start": v(-4.42, 227.25) * mm, "end": v(4.92, 227.25) * mm});
            skLineSegment(sketch, "E374", {"start": v(55.58, 227.25) * mm, "end": v(64.92, 227.25) * mm});
            skLineSegment(sketch, "E375", {"start": v(-285.58, 228.25) * mm, "end": v(-117.08, 228.25) * mm});
            skLineSegment(sketch, "E376", {"start": v(65.42, 226.75) * mm, "end": v(65.42, 225.75) * mm});
            skLineSegment(sketch, "E377", {"start": v(184.42, 194.6) * mm, "end": v(184.42, 226.25) * mm});
            skArc(sketch, "E378", {"start": v(-288.08, -225.75) * mm, "mid": v(-287.35, -227.52) * mm, "end": v(-285.58, -228.25) * mm});
            skArc(sketch, "E379", {"start": v(-285.58, -222.6) * mm, "mid": v(-287.35, -223.33) * mm, "end": v(-288.08, -225.1) * mm});
            skArc(sketch, "E380", {"start": v(-287.58, -225.75) * mm, "mid": v(-287, -227.17) * mm, "end": v(-285.58, -227.75) * mm});
            skArc(sketch, "E381", {"start": v(-285.58, -223.1) * mm, "mid": v(-287, -223.69) * mm, "end": v(-287.58, -225.1) * mm});
            skArc(sketch, "E382", {"start": v(-188.19, -184.6) * mm, "mid": v(-191.87, -185.3) * mm, "end": v(-195.04, -187.32) * mm});
            skArc(sketch, "E383", {"start": v(-188.19, -185.1) * mm, "mid": v(-191.69, -185.77) * mm, "end": v(-194.7, -187.68) * mm});
            skArc(sketch, "E384", {"start": v(-109.94, -224.75) * mm, "mid": v(-113.9, -225.53) * mm, "end": v(-117.29, -227.75) * mm});
            skArc(sketch, "E385", {"start": v(-109.94, -225.25) * mm, "mid": v(-113.77, -226.01) * mm, "end": v(-117.01, -228.18) * mm});
            skArc(sketch, "E386", {"start": v(-94.38, -224.76) * mm, "mid": v(-94.57, -224.75) * mm, "end": v(-94.75, -224.75) * mm});
            skArc(sketch, "E387", {"start": v(-94.42, -225.26) * mm, "mid": v(-94.58, -225.25) * mm, "end": v(-94.75, -225.25) * mm});
            skArc(sketch, "E388", {"start": v(-64.75, -227.24) * mm, "mid": v(-64.58, -227.25) * mm, "end": v(-64.42, -227.25) * mm});
            skArc(sketch, "E389", {"start": v(-64.71, -226.74) * mm, "mid": v(-64.57, -226.75) * mm, "end": v(-64.42, -226.75) * mm});
            skArc(sketch, "E390", {"start": v(-54.08, -224.75) * mm, "mid": v(-54.79, -225.04) * mm, "end": v(-55.08, -225.75) * mm});
            skArc(sketch, "E391", {"start": v(-54.08, -225.25) * mm, "mid": v(-54.44, -225.4) * mm, "end": v(-54.58, -225.75) * mm});
            skArc(sketch, "E392", {"start": v(-55.08, -227.25) * mm, "mid": v(-54.73, -227.1) * mm, "end": v(-54.58, -226.75) * mm});
            skArc(sketch, "E393", {"start": v(-117.25, -227.84) * mm, "mid": v(-117.22, -227.93) * mm, "end": v(-117.18, -228) * mm});
            skArc(sketch, "E394", {"start": v(-284.08, -223.1) * mm, "mid": v(-236, -213.92) * mm, "end": v(-194.7, -187.68) * mm});
            skArc(sketch, "E395", {"start": v(-284.08, -222.6) * mm, "mid": v(-236.2, -213.46) * mm, "end": v(-195.04, -187.32) * mm});
            skArc(sketch, "E396", {"start": v(-34.38, -224.76) * mm, "mid": v(-34.57, -224.75) * mm, "end": v(-34.75, -224.75) * mm});
            skArc(sketch, "E397", {"start": v(-34.42, -225.26) * mm, "mid": v(-34.58, -225.25) * mm, "end": v(-34.75, -225.25) * mm});
            skArc(sketch, "E398", {"start": v(4.92, -227.25) * mm, "mid": v(5.27, -227.1) * mm, "end": v(5.42, -226.75) * mm});
            skArc(sketch, "E399", {"start": v(-4.75, -227.24) * mm, "mid": v(-4.58, -227.25) * mm, "end": v(-4.42, -227.25) * mm});
            skArc(sketch, "E400", {"start": v(-4.71, -226.74) * mm, "mid": v(-4.57, -226.75) * mm, "end": v(-4.42, -226.75) * mm});
            skArc(sketch, "E401", {"start": v(5.92, -224.75) * mm, "mid": v(5.21, -225.04) * mm, "end": v(4.92, -225.75) * mm});
            skArc(sketch, "E402", {"start": v(5.92, -225.25) * mm, "mid": v(5.56, -225.4) * mm, "end": v(5.42, -225.75) * mm});
            skArc(sketch, "E403", {"start": v(25.62, -224.76) * mm, "mid": v(25.43, -224.75) * mm, "end": v(25.25, -224.75) * mm});
            skArc(sketch, "E404", {"start": v(25.58, -225.26) * mm, "mid": v(25.42, -225.25) * mm, "end": v(25.25, -225.25) * mm});
            skArc(sketch, "E405", {"start": v(64.92, -227.25) * mm, "mid": v(65.27, -227.1) * mm, "end": v(65.42, -226.75) * mm});
            skArc(sketch, "E406", {"start": v(55.25, -227.24) * mm, "mid": v(55.42, -227.25) * mm, "end": v(55.58, -227.25) * mm});
            skArc(sketch, "E407", {"start": v(55.29, -226.74) * mm, "mid": v(55.43, -226.75) * mm, "end": v(55.58, -226.75) * mm});
            skArc(sketch, "E408", {"start": v(65.92, -224.75) * mm, "mid": v(65.21, -225.04) * mm, "end": v(64.92, -225.75) * mm});
            skArc(sketch, "E409", {"start": v(65.92, -225.25) * mm, "mid": v(65.56, -225.4) * mm, "end": v(65.42, -225.75) * mm});
            skArc(sketch, "E410", {"start": v(182.87, -228.2) * mm, "mid": v(182.85, -227.95) * mm, "end": v(182.82, -227.7) * mm});
            skArc(sketch, "E411", {"start": v(182.87, -228.2) * mm, "mid": v(183.98, -227.5) * mm, "end": v(184.42, -226.25) * mm});
            skArc(sketch, "E412", {"start": v(182.82, -227.7) * mm, "mid": v(183.61, -227.16) * mm, "end": v(183.92, -226.25) * mm});
            skArc(sketch, "E413", {"start": v(184.42, -194.6) * mm, "mid": v(181.49, -187.53) * mm, "end": v(174.42, -184.6) * mm});
            skArc(sketch, "E414", {"start": v(183.92, -194.6) * mm, "mid": v(181.14, -187.88) * mm, "end": v(174.42, -185.1) * mm});
            skArc(sketch, "E415", {"start": v(-178.42, 38.12) * mm, "mid": v(-179.3, 40.24) * mm, "end": v(-181.42, 41.12) * mm});
            skArc(sketch, "E416", {"start": v(184.42, 48.62) * mm, "mid": v(184.27, 48.97) * mm, "end": v(183.92, 49.12) * mm});
            skArc(sketch, "E417", {"start": v(-287.58, 49.12) * mm, "mid": v(-287.94, 48.97) * mm, "end": v(-288.08, 48.62) * mm});
            skArc(sketch, "E418", {"start": v(65.42, 48.62) * mm, "mid": v(65.27, 48.97) * mm, "end": v(64.92, 49.12) * mm});
            skArc(sketch, "E419", {"start": v(5.42, 48.62) * mm, "mid": v(5.27, 48.97) * mm, "end": v(4.92, 49.12) * mm});
            skArc(sketch, "E420", {"start": v(-54.58, 48.62) * mm, "mid": v(-54.73, 48.97) * mm, "end": v(-55.08, 49.12) * mm});
            skArc(sketch, "E421", {"start": v(279.43, 41.12) * mm, "mid": v(277.31, 40.24) * mm, "end": v(276.43, 38.12) * mm});
            skArc(sketch, "E422", {"start": v(288.08, 48.62) * mm, "mid": v(287.94, 48.97) * mm, "end": v(287.58, 49.12) * mm});
            skArc(sketch, "E423", {"start": v(282.93, 49.12) * mm, "mid": v(282.58, 48.97) * mm, "end": v(282.43, 48.62) * mm});
            skArc(sketch, "E424", {"start": v(244.93, 49.12) * mm, "mid": v(244.58, 48.97) * mm, "end": v(244.43, 48.62) * mm});
            skArc(sketch, "E425", {"start": v(-156.25, 184.6) * mm, "mid": v(-165.96, 196.78) * mm, "end": v(-176.83, 207.94) * mm});
            skArc(sketch, "E426", {"start": v(-159.96, 184.6) * mm, "mid": v(-168.93, 195.6) * mm, "end": v(-178.87, 205.74) * mm});
            skArc(sketch, "E427", {"start": v(-195.04, 187.32) * mm, "mid": v(-236.2, 213.46) * mm, "end": v(-284.08, 222.6) * mm});
            skArc(sketch, "E428", {"start": v(-195.04, 187.32) * mm, "mid": v(-191.87, 185.3) * mm, "end": v(-188.19, 184.6) * mm});
            skArc(sketch, "E429", {"start": v(-117.01, 228.18) * mm, "mid": v(-113.77, 226.01) * mm, "end": v(-109.94, 225.25) * mm});
            skArc(sketch, "E430", {"start": v(-152.15, 194.87) * mm, "mid": v(-144.43, 208.26) * mm, "end": v(-157.8, 200.53) * mm});
            skArc(sketch, "E431", {"start": v(-173.42, 219.6) * mm, "mid": v(-180.87, 214.53) * mm, "end": v(-178.87, 205.74) * mm});
            skCircle(sketch, "E432", {"center": v(-150.08, 202.6) * mm, "radius": 7.25 * mm});
            skArc(sketch, "E433", {"start": v(-94.75, 225.25) * mm, "mid": v(-94.58, 225.25) * mm, "end": v(-94.42, 225.26) * mm});
            skArc(sketch, "E434", {"start": v(-64.42, 227.25) * mm, "mid": v(-64.58, 227.25) * mm, "end": v(-64.75, 227.24) * mm});
            skArc(sketch, "E435", {"start": v(-173.42, 216.6) * mm, "mid": v(-178.08, 213.43) * mm, "end": v(-176.83, 207.94) * mm});
            skArc(sketch, "E436", {"start": v(-288.08, 225.1) * mm, "mid": v(-287.35, 223.33) * mm, "end": v(-285.58, 222.6) * mm});
            skArc(sketch, "E437", {"start": v(-285.58, 228.25) * mm, "mid": v(-287.35, 227.52) * mm, "end": v(-288.08, 225.75) * mm});
            skArc(sketch, "E438", {"start": v(-54.58, 226.75) * mm, "mid": v(-54.73, 227.1) * mm, "end": v(-55.08, 227.25) * mm});
            skArc(sketch, "E439", {"start": v(-54.58, 225.75) * mm, "mid": v(-54.44, 225.4) * mm, "end": v(-54.08, 225.25) * mm});
            skArc(sketch, "E440", {"start": v(174.42, 184.6) * mm, "mid": v(181.49, 187.53) * mm, "end": v(184.42, 194.6) * mm});
            skArc(sketch, "E441", {"start": v(151.85, 194.87) * mm, "mid": v(159.57, 208.26) * mm, "end": v(146.2, 200.53) * mm});
            skCircle(sketch, "E442", {"center": v(153.92, 202.6) * mm, "radius": 7.25 * mm});
            skArc(sketch, "E443", {"start": v(-34.75, 225.25) * mm, "mid": v(-34.58, 225.25) * mm, "end": v(-34.42, 225.26) * mm});
            skArc(sketch, "E444", {"start": v(-4.42, 227.25) * mm, "mid": v(-4.58, 227.25) * mm, "end": v(-4.75, 227.24) * mm});
            skArc(sketch, "E445", {"start": v(25.25, 225.25) * mm, "mid": v(25.42, 225.25) * mm, "end": v(25.58, 225.26) * mm});
            skArc(sketch, "E446", {"start": v(55.58, 227.25) * mm, "mid": v(55.42, 227.25) * mm, "end": v(55.25, 227.24) * mm});
            skArc(sketch, "E447", {"start": v(184.42, 226.25) * mm, "mid": v(183.98, 227.5) * mm, "end": v(182.87, 228.2) * mm});
            skArc(sketch, "E448", {"start": v(5.42, 226.75) * mm, "mid": v(5.27, 227.1) * mm, "end": v(4.92, 227.25) * mm});
            skArc(sketch, "E449", {"start": v(65.42, 226.75) * mm, "mid": v(65.27, 227.1) * mm, "end": v(64.92, 227.25) * mm});
            skArc(sketch, "E450", {"start": v(65.42, 225.75) * mm, "mid": v(65.56, 225.4) * mm, "end": v(65.92, 225.25) * mm});
            skArc(sketch, "E451", {"start": v(5.42, 225.75) * mm, "mid": v(5.56, 225.4) * mm, "end": v(5.92, 225.25) * mm});
            skLineSegment(sketch, "E452", {"start": v(-117.08, -228.25) * mm, "end": v(-117.13, -228.14) * mm});
            skLineSegment(sketch, "E453", {"start": v(-117.13, -228.14) * mm, "end": v(-117.18, -228) * mm});
            skFitSpline(sketch, "E454", {"points": [v(95.92, -225.25) * mm, v(95.92, -225.24) * mm, v(95.91, -225.07) * mm, v(95.92, -224.9) * mm, v(95.93, -224.75) * mm]});
            skLineSegment(sketch, "E455", {"start": v(-117.25, -227.84) * mm, "end": v(-117.29, -227.75) * mm});
            skFitSpline(sketch, "E456", {"points": [v(247.51, 49.12) * mm, v(247.41, 49.12) * mm, v(247.2, 48.97) * mm, v(247.15, 48.74) * mm, v(247.15, 48.62) * mm]});
            skFitSpline(sketch, "E457", {"points": [v(265.57, 41.12) * mm, v(265.86, 41.12) * mm, v(266.48, 40.94) * mm, v(267.2, 40.24) * mm, v(267.67, 39.26) * mm, v(267.77, 38.5) * mm, v(267.77, 38.12) * mm]});
            skSolve(sketch);
        }
        {
            var Q0;
            Q0=qCreatedBy(makeId("Front.planeOp"),FACE);
            var sketch = newSketch(context, id + "F1", { "sketchPlane" : qUnion([Q0])});
            skLineSegment(sketch, "E458", {"start": v(-188.19, 184.6) * mm, "end": v(174.42, 184.6) * mm});
            skLineSegment(sketch, "E459", {"start": v(184.42, 226.18) * mm, "end": v(184.42, 194.6) * mm});
            skLineSegment(sketch, "E460", {"start": v(-285.58, 228.25) * mm, "end": v(-117.08, 228.25) * mm});
            skArc(sketch, "E461", {"start": v(-195.04, 187.32) * mm, "mid": v(-236.88, 213.73) * mm, "end": v(-285.55, 222.6) * mm});
            skLineSegment(sketch, "E462", {"start": v(-288.08, 225.75) * mm, "end": v(-288.08, 225.1) * mm});
            skPoint(sketch, "E463.visualSharp", {"position": v(-192.23, 184.6) * mm});
            skArc(sketch, "E463.filletArc", {"start": v(-195.04, 187.32) * mm, "mid": v(-191.87, 185.3) * mm, "end": v(-188.19, 184.6) * mm});
            skArc(sketch, "E464.filletArc", {"start": v(-288.08, 225.1) * mm, "mid": v(-287.34, 223.32) * mm, "end": v(-285.55, 222.6) * mm});
            skArc(sketch, "E465.filletArc", {"start": v(-285.58, 228.25) * mm, "mid": v(-287.35, 227.52) * mm, "end": v(-288.08, 225.75) * mm});
            skLineSegment(sketch, "E466", {"start": v(95.92, 225.25) * mm, "end": v(182.35, 228.18) * mm});
            skArc(sketch, "E467.filletArc", {"start": v(184.42, 226.18) * mm, "mid": v(183.8, 227.62) * mm, "end": v(182.35, 228.18) * mm});
            skLineSegment(sketch, "E468", {"start": v(65.92, 225.25) * mm, "end": v(95.92, 225.25) * mm});
            skLineSegment(sketch, "E469", {"start": v(65.42, 226.75) * mm, "end": v(65.42, 225.75) * mm});
            skLineSegment(sketch, "E470", {"start": v(5.42, 226.75) * mm, "end": v(5.42, 225.75) * mm});
            skLineSegment(sketch, "E471", {"start": v(-54.58, 226.75) * mm, "end": v(-54.58, 225.75) * mm});
            skLineSegment(sketch, "E472", {"start": v(-109.94, 225.25) * mm, "end": v(-94.75, 225.25) * mm});
            skLineSegment(sketch, "E473", {"start": v(-64.42, 227.25) * mm, "end": v(-55.08, 227.25) * mm});
            skLineSegment(sketch, "E474", {"start": v(-54.08, 225.25) * mm, "end": v(-34.75, 225.25) * mm});
            skLineSegment(sketch, "E475", {"start": v(-4.42, 227.25) * mm, "end": v(4.92, 227.25) * mm});
            skLineSegment(sketch, "E476", {"start": v(5.92, 225.25) * mm, "end": v(25.25, 225.25) * mm});
            skLineSegment(sketch, "E477", {"start": v(55.58, 227.25) * mm, "end": v(64.92, 227.25) * mm});
            skLineSegment(sketch, "E478", {"start": v(-94.42, 225.26) * mm, "end": v(-64.75, 227.24) * mm});
            skArc(sketch, "E479.filletArc", {"start": v(-94.75, 225.25) * mm, "mid": v(-94.58, 225.25) * mm, "end": v(-94.42, 225.26) * mm});
            skArc(sketch, "E480.filletArc", {"start": v(-64.42, 227.25) * mm, "mid": v(-64.58, 227.25) * mm, "end": v(-64.75, 227.24) * mm});
            skArc(sketch, "E481", {"start": v(-117.08, 228.25) * mm, "mid": v(-113.81, 226.03) * mm, "end": v(-109.94, 225.25) * mm});
            skArc(sketch, "E482.filletArc", {"start": v(-54.58, 226.75) * mm, "mid": v(-54.73, 227.1) * mm, "end": v(-55.08, 227.25) * mm});
            skArc(sketch, "E483.filletArc", {"start": v(-54.58, 225.75) * mm, "mid": v(-54.44, 225.4) * mm, "end": v(-54.08, 225.25) * mm});
            skArc(sketch, "E484.filletArc", {"start": v(5.42, 226.75) * mm, "mid": v(5.27, 227.1) * mm, "end": v(4.92, 227.25) * mm});
            skArc(sketch, "E485.filletArc", {"start": v(5.42, 225.75) * mm, "mid": v(5.56, 225.4) * mm, "end": v(5.92, 225.25) * mm});
            skArc(sketch, "E486.filletArc", {"start": v(65.42, 226.75) * mm, "mid": v(65.27, 227.1) * mm, "end": v(64.92, 227.25) * mm});
            skArc(sketch, "E487.filletArc", {"start": v(65.42, 225.75) * mm, "mid": v(65.56, 225.4) * mm, "end": v(65.92, 225.25) * mm});
            skLineSegment(sketch, "E488", {"start": v(-34.42, 225.26) * mm, "end": v(-4.75, 227.24) * mm});
            skArc(sketch, "E489.filletArc", {"start": v(-34.75, 225.25) * mm, "mid": v(-34.58, 225.25) * mm, "end": v(-34.42, 225.26) * mm});
            skArc(sketch, "E490.filletArc", {"start": v(-4.42, 227.25) * mm, "mid": v(-4.58, 227.25) * mm, "end": v(-4.75, 227.24) * mm});
            skLineSegment(sketch, "E491", {"start": v(25.58, 225.26) * mm, "end": v(55.25, 227.24) * mm});
            skArc(sketch, "E492.filletArc", {"start": v(25.25, 225.25) * mm, "mid": v(25.42, 225.25) * mm, "end": v(25.58, 225.26) * mm});
            skArc(sketch, "E493.filletArc", {"start": v(55.58, 227.25) * mm, "mid": v(55.42, 227.25) * mm, "end": v(55.25, 227.24) * mm});
            skArc(sketch, "E494.filletArc", {"start": v(174.42, 184.6) * mm, "mid": v(181.49, 187.53) * mm, "end": v(184.42, 194.6) * mm});
            skSolve(sketch);
        }
        {
            var Q0;
            Q0 = qSketchRegion(id + "F1", true);
            extrude(context, id + "F2", {"entities" : qUnion([Q0]), "oppositeDirection" : true, "depth" : 20 * mm});
        }
        {
            var Q0;
            Q0=makeQuery(id+"F2.opExtrude","CAP_FACE",FACE,{"disambiguationData":[OSD([sQuery(id+"F1.wireOp",EDGE,"E458"),sQuery(id+"F1.wireOp",EDGE,"E459"),sQuery(id+"F1.wireOp",EDGE,"E460"),sQuery(id+"F1.wireOp",EDGE,"E461"),sQuery(id+"F1.wireOp",EDGE,"E462"),sQuery(id+"F1.wireOp",EDGE,"E463.filletArc"),sQuery(id+"F1.wireOp",EDGE,"E464.filletArc"),sQuery(id+"F1.wireOp",EDGE,"E465.filletArc"),sQuery(id+"F1.wireOp",EDGE,"E466"),sQuery(id+"F1.wireOp",EDGE,"E467.filletArc"),sQuery(id+"F1.wireOp",EDGE,"E468"),sQuery(id+"F1.wireOp",EDGE,"E469"),sQuery(id+"F1.wireOp",EDGE,"E470"),sQuery(id+"F1.wireOp",EDGE,"E471"),sQuery(id+"F1.wireOp",EDGE,"E472"),sQuery(id+"F1.wireOp",EDGE,"E473"),sQuery(id+"F1.wireOp",EDGE,"E474"),sQuery(id+"F1.wireOp",EDGE,"E475"),sQuery(id+"F1.wireOp",EDGE,"E476"),sQuery(id+"F1.wireOp",EDGE,"E477"),sQuery(id+"F1.wireOp",EDGE,"E478"),sQuery(id+"F1.wireOp",EDGE,"E479.filletArc"),sQuery(id+"F1.wireOp",EDGE,"E480.filletArc"),sQuery(id+"F1.wireOp",EDGE,"E481"),sQuery(id+"F1.wireOp",EDGE,"E482.filletArc"),sQuery(id+"F1.wireOp",EDGE,"E483.filletArc"),sQuery(id+"F1.wireOp",EDGE,"E484.filletArc"),sQuery(id+"F1.wireOp",EDGE,"E485.filletArc"),sQuery(id+"F1.wireOp",EDGE,"E486.filletArc"),sQuery(id+"F1.wireOp",EDGE,"E487.filletArc"),sQuery(id+"F1.wireOp",EDGE,"E488"),sQuery(id+"F1.wireOp",EDGE,"E489.filletArc"),sQuery(id+"F1.wireOp",EDGE,"E490.filletArc"),sQuery(id+"F1.wireOp",EDGE,"E491"),sQuery(id+"F1.wireOp",EDGE,"E492.filletArc"),sQuery(id+"F1.wireOp",EDGE,"E493.filletArc"),sQuery(id+"F1.wireOp",EDGE,"E494.filletArc")])],"isStart":true});
            var sketch = newSketch(context, id + "F3", { "sketchPlane" : qUnion([Q0])});
            skLineSegment(sketch, "E495.bottom", {"start": v(-301.72, 261.53) * mm, "end": v(282.32, 261.53) * mm});
            skLineSegment(sketch, "E495.top", {"start": v(-301.72, 103.04) * mm, "end": v(282.32, 103.04) * mm});
            skLineSegment(sketch, "E495.left", {"start": v(-301.72, 261.53) * mm, "end": v(-301.72, 103.04) * mm});
            skLineSegment(sketch, "E495.right", {"start": v(282.32, 261.53) * mm, "end": v(282.32, 103.04) * mm});
            skArc(sketch, "E496.0", {"start": v(-156.25, 184.6) * mm, "mid": v(-165.96, 196.78) * mm, "end": v(-176.83, 207.94) * mm});
            skArc(sketch, "E497.0", {"start": v(-173.42, 216.6) * mm, "mid": v(-178.08, 213.43) * mm, "end": v(-176.83, 207.94) * mm});
            skLineSegment(sketch, "E498.0", {"start": v(184.42, 216.6) * mm, "end": v(-173.42, 216.6) * mm});
            skLineSegment(sketch, "E499.0", {"start": v(184.42, 194.6) * mm, "end": v(184.42, 226.25) * mm});
            skArc(sketch, "E500.0", {"start": v(174.42, 184.6) * mm, "mid": v(181.49, 187.53) * mm, "end": v(184.42, 194.6) * mm});
            skLineSegment(sketch, "E501.0", {"start": v(-156.25, 184.6) * mm, "end": v(174.42, 184.6) * mm});
            skPoint(sketch, "E502.orphan", {"position": v(-188.19, 184.6) * mm});
            skSolve(sketch);
        }
        {
            var Q0;
            Q0 = qSketchRegion(id + "F3", true);
            extrude(context, id + "F4", {"entities" : qUnion([Q0]), "operationType" : NewBodyOperationType.REMOVE, "oppositeDirection" : true, "depth" : 12 * mm});
        }
        {
            var Q0;
            Q0=makeQuery(id+"F4.boolean.opBoolean","COPY",EDGE,{"derivedFrom":makeQuery(id+"F4.opExtrude","CAP_EDGE",EDGE,{"disambiguationData":[OSD([sQuery(id+"F3.wireOp",EDGE,"E496.0")])],"isStart":false})});
            fillet(context, id + "F5", {"entities" : qUnion([Q0]), "radius" : 3 * mm, "tangentPropagation" : true, "allowEdgeOverflow" : false});
        }
        {
            var Q0;
            Q0=sQuery(id+"F0.wireOp",VERTEX,"E430.center");
            var Q1;
            Q1=sQuery(id+"F0.wireOp",VERTEX,"E441.center");
            var Q2;
            Q2=makeQuery(id+"F2.opExtrude","SWEPT_BODY",BODY,{"disambiguationData":[OSD([sQuery(id+"F1.wireOp",EDGE,"E458"),sQuery(id+"F1.wireOp",EDGE,"E459"),sQuery(id+"F1.wireOp",EDGE,"E460"),sQuery(id+"F1.wireOp",EDGE,"E461"),sQuery(id+"F1.wireOp",EDGE,"E462"),sQuery(id+"F1.wireOp",EDGE,"E463.filletArc"),sQuery(id+"F1.wireOp",EDGE,"E464.filletArc"),sQuery(id+"F1.wireOp",EDGE,"E465.filletArc"),sQuery(id+"F1.wireOp",EDGE,"E466"),sQuery(id+"F1.wireOp",EDGE,"E467.filletArc"),sQuery(id+"F1.wireOp",EDGE,"E468"),sQuery(id+"F1.wireOp",EDGE,"E469"),sQuery(id+"F1.wireOp",EDGE,"E470"),sQuery(id+"F1.wireOp",EDGE,"E471"),sQuery(id+"F1.wireOp",EDGE,"E472"),sQuery(id+"F1.wireOp",EDGE,"E473"),sQuery(id+"F1.wireOp",EDGE,"E474"),sQuery(id+"F1.wireOp",EDGE,"E475"),sQuery(id+"F1.wireOp",EDGE,"E476"),sQuery(id+"F1.wireOp",EDGE,"E477"),sQuery(id+"F1.wireOp",EDGE,"E478"),sQuery(id+"F1.wireOp",EDGE,"E479.filletArc"),sQuery(id+"F1.wireOp",EDGE,"E480.filletArc"),sQuery(id+"F1.wireOp",EDGE,"E481"),sQuery(id+"F1.wireOp",EDGE,"E482.filletArc"),sQuery(id+"F1.wireOp",EDGE,"E483.filletArc"),sQuery(id+"F1.wireOp",EDGE,"E484.filletArc"),sQuery(id+"F1.wireOp",EDGE,"E485.filletArc"),sQuery(id+"F1.wireOp",EDGE,"E486.filletArc"),sQuery(id+"F1.wireOp",EDGE,"E487.filletArc"),sQuery(id+"F1.wireOp",EDGE,"E488"),sQuery(id+"F1.wireOp",EDGE,"E489.filletArc"),sQuery(id+"F1.wireOp",EDGE,"E490.filletArc"),sQuery(id+"F1.wireOp",EDGE,"E491"),sQuery(id+"F1.wireOp",EDGE,"E492.filletArc"),sQuery(id+"F1.wireOp",EDGE,"E493.filletArc"),sQuery(id+"F1.wireOp",EDGE,"E494.filletArc")])]});
            hole(context, id + "F6", {"style" : HoleStyle.SIMPLE, "endStyle" : HoleEndStyle.BLIND, "standardTappedOrClearance" : lookupTablePath({ "standard" : "ISO", "engagement" : "75%", "pitch" : "1.5 mm", "size" : "M16", "type" : "Tapped" }), "standardBlindInLast" : lookupTablePath({ "standard" : "ISO", "engagement" : "75%", "pitch" : "1.5 mm", "size" : "M16", "type" : "Tapped" }), "holeDiameter" : 14.5 * mm, "holeDepth" : 10 * mm, "startFromSketch" : true, "locations" : qUnion([Q0, Q1]), "scope" : qUnion([Q2]), "majorDiameter" : 16 * mm});
        }
        {
            var Q0;
            Q0=makeQuery(id+"F2.opExtrude","CAP_EDGE",EDGE,{"disambiguationData":[OSD([sQuery(id+"F1.wireOp",EDGE,"E458")])],"isStart":false});
            var Q1;
            Q1=makeQuery(id+"F2.opExtrude","CAP_EDGE",EDGE,{"disambiguationData":[OSD([sQuery(id+"F1.wireOp",EDGE,"E468")])],"isStart":false});
            var Q2;
            Q2=makeQuery(id+"F2.opExtrude","CAP_EDGE",EDGE,{"disambiguationData":[OSD([sQuery(id+"F1.wireOp",EDGE,"E477")])],"isStart":false});
            fillet(context, id + "F7", {"entities" : qUnion([Q0, Q1, Q2]), "radius" : .5 * mm, "tangentPropagation" : true, "allowEdgeOverflow" : false});
        }
        {
            var Q0;
            Q0=makeQuery(id+"F2.opExtrude","CAP_FACE",FACE,{"disambiguationData":[OSD([sQuery(id+"F1.wireOp",EDGE,"E458"),sQuery(id+"F1.wireOp",EDGE,"E459"),sQuery(id+"F1.wireOp",EDGE,"E460"),sQuery(id+"F1.wireOp",EDGE,"E461"),sQuery(id+"F1.wireOp",EDGE,"E462"),sQuery(id+"F1.wireOp",EDGE,"E463.filletArc"),sQuery(id+"F1.wireOp",EDGE,"E464.filletArc"),sQuery(id+"F1.wireOp",EDGE,"E465.filletArc"),sQuery(id+"F1.wireOp",EDGE,"E466"),sQuery(id+"F1.wireOp",EDGE,"E467.filletArc"),sQuery(id+"F1.wireOp",EDGE,"E468"),sQuery(id+"F1.wireOp",EDGE,"E469"),sQuery(id+"F1.wireOp",EDGE,"E470"),sQuery(id+"F1.wireOp",EDGE,"E471"),sQuery(id+"F1.wireOp",EDGE,"E472"),sQuery(id+"F1.wireOp",EDGE,"E473"),sQuery(id+"F1.wireOp",EDGE,"E474"),sQuery(id+"F1.wireOp",EDGE,"E475"),sQuery(id+"F1.wireOp",EDGE,"E476"),sQuery(id+"F1.wireOp",EDGE,"E477"),sQuery(id+"F1.wireOp",EDGE,"E478"),sQuery(id+"F1.wireOp",EDGE,"E479.filletArc"),sQuery(id+"F1.wireOp",EDGE,"E480.filletArc"),sQuery(id+"F1.wireOp",EDGE,"E481"),sQuery(id+"F1.wireOp",EDGE,"E482.filletArc"),sQuery(id+"F1.wireOp",EDGE,"E483.filletArc"),sQuery(id+"F1.wireOp",EDGE,"E484.filletArc"),sQuery(id+"F1.wireOp",EDGE,"E485.filletArc"),sQuery(id+"F1.wireOp",EDGE,"E486.filletArc"),sQuery(id+"F1.wireOp",EDGE,"E487.filletArc"),sQuery(id+"F1.wireOp",EDGE,"E488"),sQuery(id+"F1.wireOp",EDGE,"E489.filletArc"),sQuery(id+"F1.wireOp",EDGE,"E490.filletArc"),sQuery(id+"F1.wireOp",EDGE,"E491"),sQuery(id+"F1.wireOp",EDGE,"E492.filletArc"),sQuery(id+"F1.wireOp",EDGE,"E493.filletArc"),sQuery(id+"F1.wireOp",EDGE,"E494.filletArc")])],"isStart":false});
            var sketch = newSketch(context, id + "F8", { "sketchPlane" : qUnion([Q0])});
            skText(sketch, "E503", { "text": "20ml (B)", "fontName": "OpenSans-Regular.ttf"});
            const initialGuessF8  = {"E503": [-0.0734, 0.19763, 1, 0, 0.01085]};
            skSetInitialGuess(sketch, initialGuessF8);
            skSolve(sketch);
        }
        {
            var Q0;
            Q0=makeQuery(id+"F8.imprint","IMPRINT",FACE,{"disambiguationData":[TD([[makeQuery(id+"F8.imprint","IMPRINT",EDGE,{"derivedFrom":sQuery(id+"F8.wireOp",EDGE,"E503.sketch_text.stroke-20")}),-1.0]])]});
            var Q1;
            Q1=makeQuery(id+"F8.imprint","IMPRINT",FACE,{"disambiguationData":[TD([[makeQuery(id+"F8.imprint","IMPRINT",EDGE,{"derivedFrom":sQuery(id+"F8.wireOp",EDGE,"E503.sketch_text.stroke-0")}),-1.0]])]});
            var Q2;
            Q2=makeQuery(id+"F8.imprint","IMPRINT",FACE,{"disambiguationData":[TD([[makeQuery(id+"F8.imprint","IMPRINT",EDGE,{"derivedFrom":sQuery(id+"F8.wireOp",EDGE,"E503.sketch_text.stroke-36")}),-1.0]])]});
            var Q3;
            Q3=makeQuery(id+"F8.imprint","IMPRINT",FACE,{"disambiguationData":[TD([[makeQuery(id+"F8.imprint","IMPRINT",EDGE,{"derivedFrom":sQuery(id+"F8.wireOp",EDGE,"E503.sketch_text.stroke-64")}),-1.0]])]});
            var Q4;
            Q4=makeQuery(id+"F8.imprint","IMPRINT",FACE,{"disambiguationData":[TD([[makeQuery(id+"F8.imprint","IMPRINT",EDGE,{"derivedFrom":sQuery(id+"F8.wireOp",EDGE,"E503.sketch_text.stroke-68")}),-1.0]])]});
            var Q5;
            Q5=makeQuery(id+"F8.imprint","IMPRINT",FACE,{"disambiguationData":[TD([[makeQuery(id+"F8.imprint","IMPRINT",EDGE,{"derivedFrom":sQuery(id+"F8.wireOp",EDGE,"E503.sketch_text.stroke-78")}),-1.0]])]});
            var Q6;
            Q6=makeQuery(id+"F8.imprint","IMPRINT",FACE,{"disambiguationData":[TD([[makeQuery(id+"F8.imprint","IMPRINT",EDGE,{"derivedFrom":sQuery(id+"F8.wireOp",EDGE,"E503.sketch_text.stroke-103")}),-1.0]])]});
            extrude(context, id + "F9", {"entities" : qUnion([Q0, Q1, Q2, Q3, Q4, Q5, Q6]), "operationType" : NewBodyOperationType.REMOVE, "oppositeDirection" : true, "depth" : 0.13 * mm});
        }
    });
